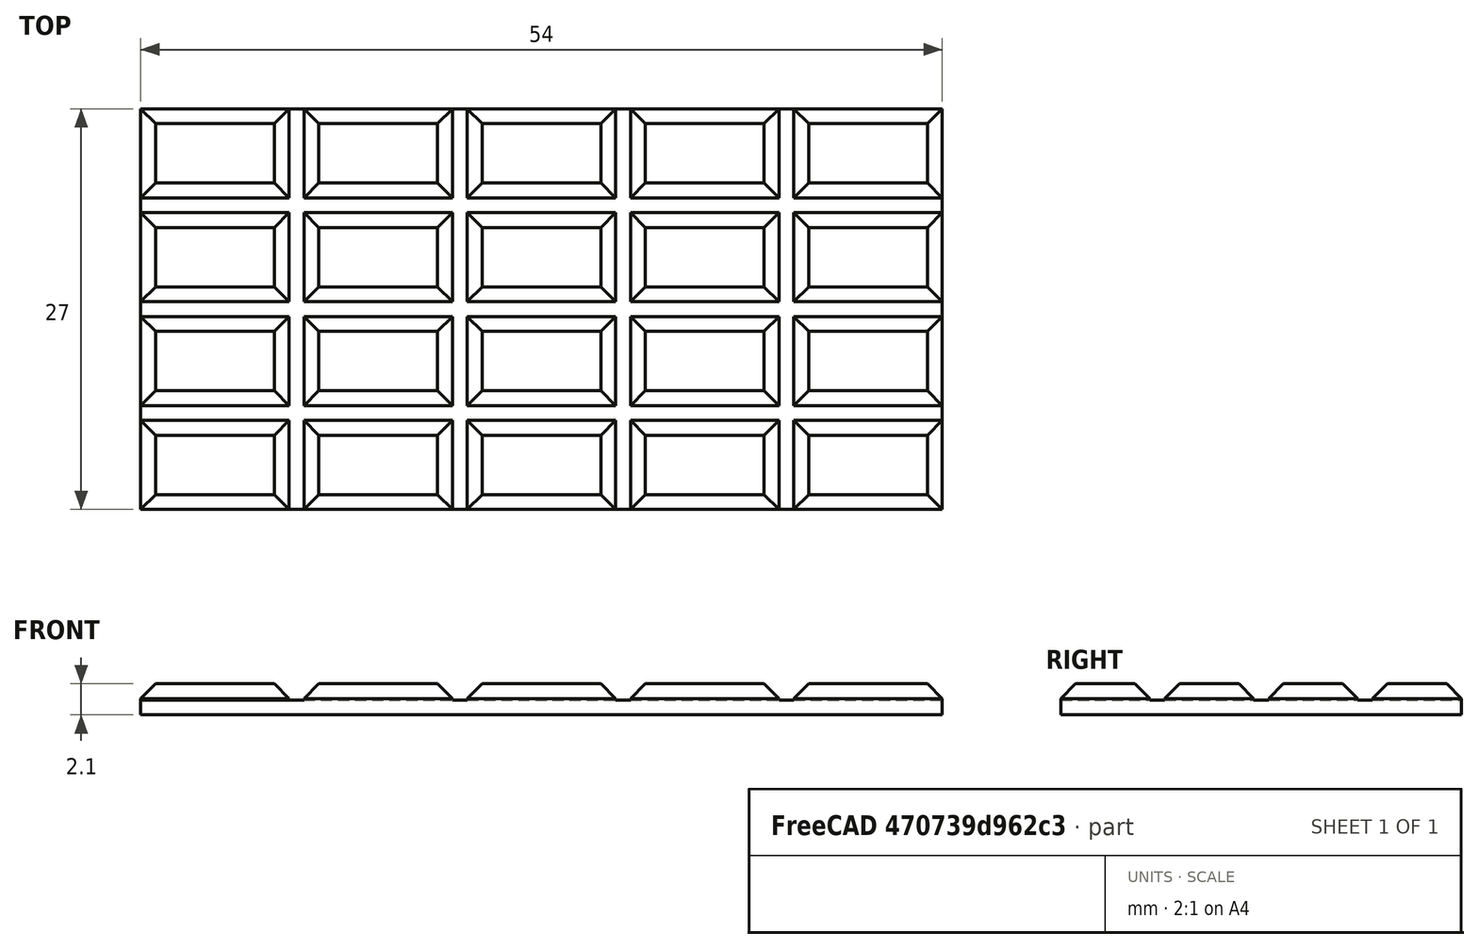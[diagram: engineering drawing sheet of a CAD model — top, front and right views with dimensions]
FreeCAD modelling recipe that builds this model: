
FCSTD DOCUMENT  (FreeCAD 0.21R33771 (Git))
Label: OJT1_T12R02_xocolata
License: All rights reserved
LicenseURL: http://en.wikipedia.org/wiki/All_rights_reserved
objects: Part::Box×2, Part::Chamfer×1, Part::FeaturePython×1, Part::MultiFuse×1
note: 4 computed .brp shape members not serialized (recipe doc carries the construction recipe); baked Part::Feature solids carry a one-line shape summary decoded from their .brp

FEATURE [Part::Box] Box  label="Cube"
  AttacherType = Attacher::AttachEngine3D
  Height = 1
  Length = 54
  Width = 27
FEATURE [Part::Box] Box001  label="Cube001"
  AttacherType = Attacher::AttachEngine3D
  Height = 1.1
  Length = 10
  Placement = pos=(0,0,1) rot=(0,0,1;0rad)
  Width = 6
FEATURE [Part::Chamfer] Chamfer
  Base = -> Box001
  Edges = 4 edges r=1: [Edge2,Edge6,Edge10,Edge12]
FEATURE [Part::FeaturePython] Array  # Draft array (typed FeaturePython)
  AlwaysSyncPlacement = false
  Angle = 360
  ArrayType = 0
  Axis = (0,0,1)
  Base = -> Chamfer
  Center = (0,0,0)
  Count = 20
  ExpandArray = false
  Fuse = false
  IntervalAxis = (0,0,0)
  IntervalX = (11,0,0)
  IntervalY = (0,7,0)
  IntervalZ = (0,0,100)
  NumberCircles = 3
  NumberPolar = 5
  NumberX = 5
  NumberY = 4
  NumberZ = 1
  PlacementList = 20 placements: [(0,0,0),(0,7,0),(0,14,0),(0,21,0),(11,0,0),(11,7,0),(11,14,0),(11,21,0),(22,0,0),(22,7,0),(22,14,0),(22,21,0),(33,0,0),(33,7,0),(33,14,0),(33,21,0),(44,0,0),(44,7,0),(44,14,0),(44,21,0)]
  RadialDistance = 50
  ScaleList = (20) [(1,1,1),(1,1,1),(1,1,1),(1,1,1),(1,1,1),(1,1,1),(1,1,1),(1,1,1),(1,1,1),(1,1,1),(1,1,1),(1,1,1),(1,1,1),(1,1,1),(1,1,1),(1,1,1),(1,1,1),(1,1,1),(1,1,1),(1,1,1)]
  Symmetry = 1
  TangentialDistance = 25
FEATURE [Part::MultiFuse] Fusion
  Refine = true
  Shapes = -> [Box,Array]
